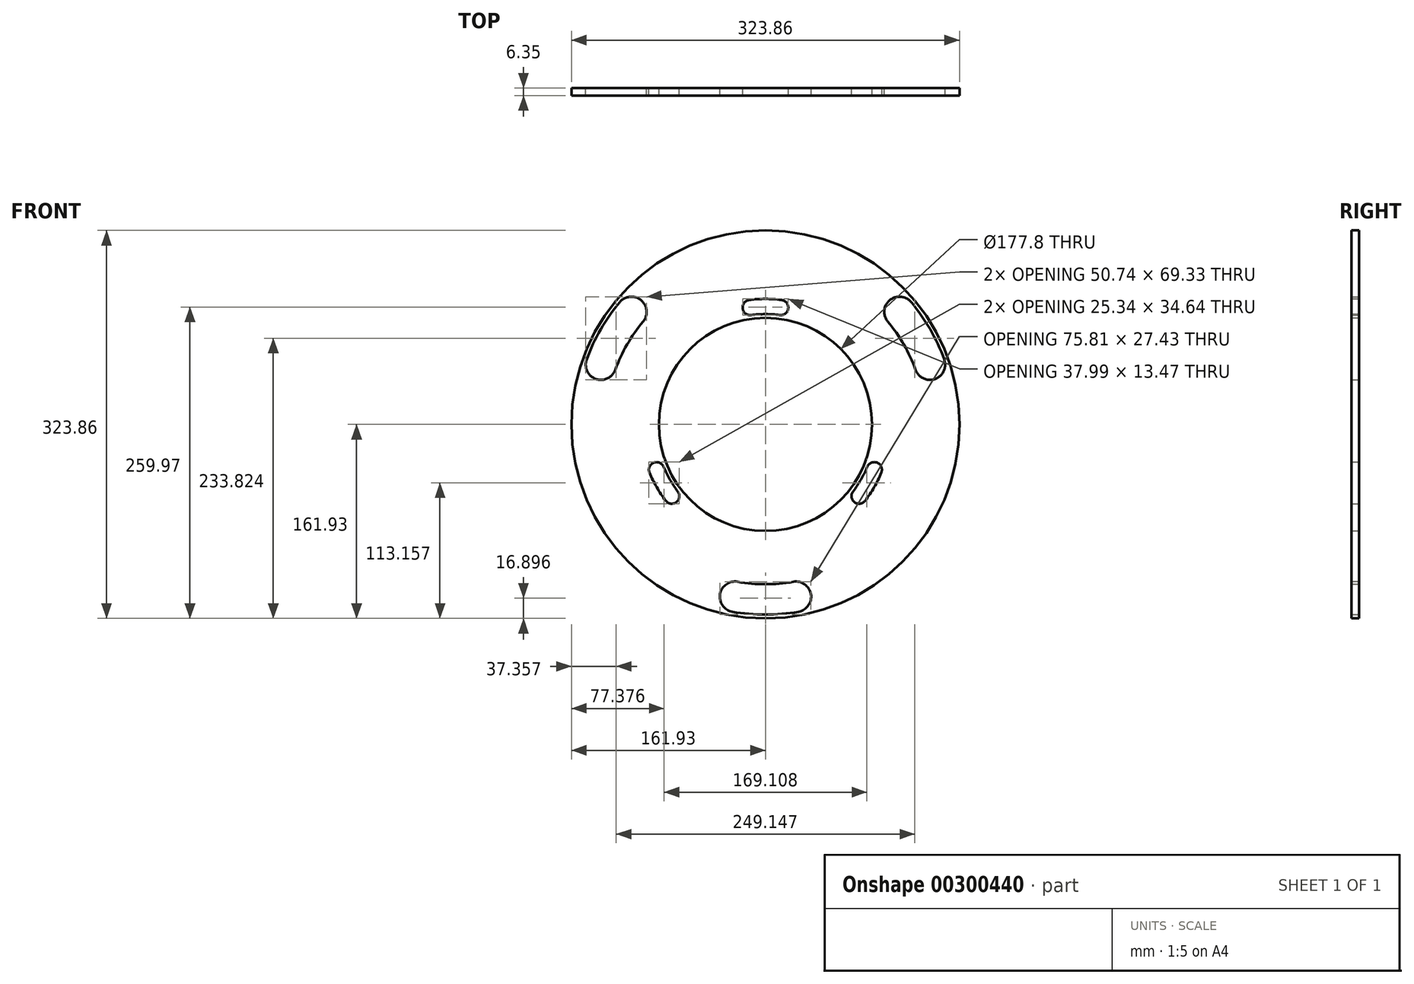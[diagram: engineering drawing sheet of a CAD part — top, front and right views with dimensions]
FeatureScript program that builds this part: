
annotation { "Feature Type Name" : "Feature", "Feature Type Description" : "" }
export const myFeature = defineFeature(function(context is Context, id is Id, definition is map)
    precondition{}
    {
        {
            var Q0;
            Q0=qCreatedBy(makeId("Front.planeOp"),FACE);
            var sketch = newSketch(context, id + "F0", { "sketchPlane" : qUnion([Q0])});
            skCircle(sketch, "E0", {"center": v(0, 0) * mm, "radius": 88.9 * mm});
            skCircle(sketch, "E1", {"center": v(0, 0) * mm, "radius": 161.93 * mm});
            skLineSegment(sketch, "E2", {"start": v(0, -179) * mm, "end": v(0, 179) * mm, "construction": true});
            skLineSegment(sketch, "E3", {"start": v(-182.42, 0) * mm, "end": v(202.22, 0) * mm, "construction": true});
            skLineSegment(sketch, "E4", {"start": v(-171.56, 99.05) * mm, "end": v(180.63, -104.28) * mm, "construction": true});
            skArc(sketch, "E5.0", {"start": v(-121.58, 102.08) * mm, "mid": v(-137.48, 79.38) * mm, "end": v(-149.2, 54.26) * mm});
            skArc(sketch, "E6.0", {"start": v(-102.13, 85.74) * mm, "mid": v(-115.48, 66.68) * mm, "end": v(-125.32, 45.57) * mm});
            skLineSegment(sketch, "E7", {"start": v(0, 104.78) * mm, "end": v(0, 92.08) * mm, "construction": true});
            skLineSegment(sketch, "E8", {"start": v(0, 133.35) * mm, "end": v(0, 158.75) * mm, "construction": true});
            skPoint(sketch, "E9", {"position": v(0, 98.43) * mm});
            skPoint(sketch, "E10", {"position": v(0, 146.05) * mm});
            skCircle(sketch, "E11", {"center": v(0, 0) * mm, "radius": 98.43 * mm, "construction": true});
            skCircle(sketch, "E12", {"center": v(0, 0) * mm, "radius": 146.05 * mm, "construction": true});
            skArc(sketch, "E13", {"start": v(-149.2, 54.26) * mm, "mid": v(-141.6, 37.98) * mm, "end": v(-125.32, 45.57) * mm});
            skArc(sketch, "E14", {"start": v(-102.13, 85.74) * mm, "mid": v(-103.69, 103.64) * mm, "end": v(-121.58, 102.08) * mm});
            skArc(sketch, "E15", {"start": v(-13.52, 103.9) * mm, "mid": v(-19, 96.78) * mm, "end": v(-11.88, 91.3) * mm});
            skArc(sketch, "E16", {"start": v(11.88, 91.3) * mm, "mid": v(19, 96.78) * mm, "end": v(13.52, 103.9) * mm});
            skArc(sketch, "E17.trimOffspring", {"start": v(11.88, 91.3) * mm, "mid": v(0, 92.08) * mm, "end": v(-11.88, 91.3) * mm});
            skArc(sketch, "E18.trimOffspring", {"start": v(13.52, 103.9) * mm, "mid": v(0, 104.77) * mm, "end": v(-13.52, 103.9) * mm});
            skArc(sketch, "E19.1.0", {"start": v(-96.74, -40.24) * mm, "mid": v(-90.74, -52.39) * mm, "end": v(-83.22, -63.66) * mm});
            skArc(sketch, "E19.1.1", {"start": v(-85.01, -35.36) * mm, "mid": v(-93.31, -31.94) * mm, "end": v(-96.74, -40.24) * mm});
            skArc(sketch, "E19.1.2", {"start": v(-85.01, -35.36) * mm, "mid": v(-79.74, -46.04) * mm, "end": v(-73.13, -55.94) * mm});
            skArc(sketch, "E19.1.3", {"start": v(-83.22, -63.66) * mm, "mid": v(-74.32, -64.84) * mm, "end": v(-73.13, -55.94) * mm});
            skArc(sketch, "E19.2.0", {"start": v(83.22, -63.66) * mm, "mid": v(90.74, -52.39) * mm, "end": v(96.74, -40.24) * mm});
            skArc(sketch, "E19.2.1", {"start": v(73.13, -55.94) * mm, "mid": v(74.32, -64.84) * mm, "end": v(83.22, -63.66) * mm});
            skArc(sketch, "E19.2.2", {"start": v(73.13, -55.94) * mm, "mid": v(79.74, -46.04) * mm, "end": v(85.01, -35.36) * mm});
            skArc(sketch, "E19.2.3", {"start": v(96.74, -40.24) * mm, "mid": v(93.31, -31.94) * mm, "end": v(85.01, -35.36) * mm});
            skArc(sketch, "E20.1.0", {"start": v(-27.6, -156.33) * mm, "mid": v(0, -158.75) * mm, "end": v(27.6, -156.33) * mm});
            skArc(sketch, "E20.1.1", {"start": v(-23.2, -131.32) * mm, "mid": v(-37.9, -141.62) * mm, "end": v(-27.6, -156.33) * mm});
            skArc(sketch, "E20.1.2", {"start": v(-23.2, -131.32) * mm, "mid": v(0, -133.35) * mm, "end": v(23.2, -131.32) * mm});
            skArc(sketch, "E20.1.3", {"start": v(27.6, -156.33) * mm, "mid": v(37.9, -141.62) * mm, "end": v(23.2, -131.32) * mm});
            skArc(sketch, "E20.2.0", {"start": v(149.2, 54.26) * mm, "mid": v(137.48, 79.38) * mm, "end": v(121.58, 102.08) * mm});
            skArc(sketch, "E20.2.1", {"start": v(125.32, 45.57) * mm, "mid": v(141.6, 37.98) * mm, "end": v(149.2, 54.26) * mm});
            skArc(sketch, "E20.2.2", {"start": v(125.32, 45.57) * mm, "mid": v(115.48, 66.67) * mm, "end": v(102.13, 85.74) * mm});
            skArc(sketch, "E20.2.3", {"start": v(121.58, 102.08) * mm, "mid": v(103.69, 103.64) * mm, "end": v(102.13, 85.74) * mm});
            skSolve(sketch);
        }
        {
            var Q0;
            Q0=makeQuery(id+"F0.imprint","IMPRINT",FACE,{"disambiguationData":[TD([[makeQuery(id+"F0.imprint","IMPRINT",EDGE,{"derivedFrom":sQuery(id+"F0.wireOp",EDGE,"E0")}),-1.0]])]});
            extrude(context, id + "F1", {"entities" : qUnion([Q0]), "depth" : 6.35 * mm});
        }
    });
